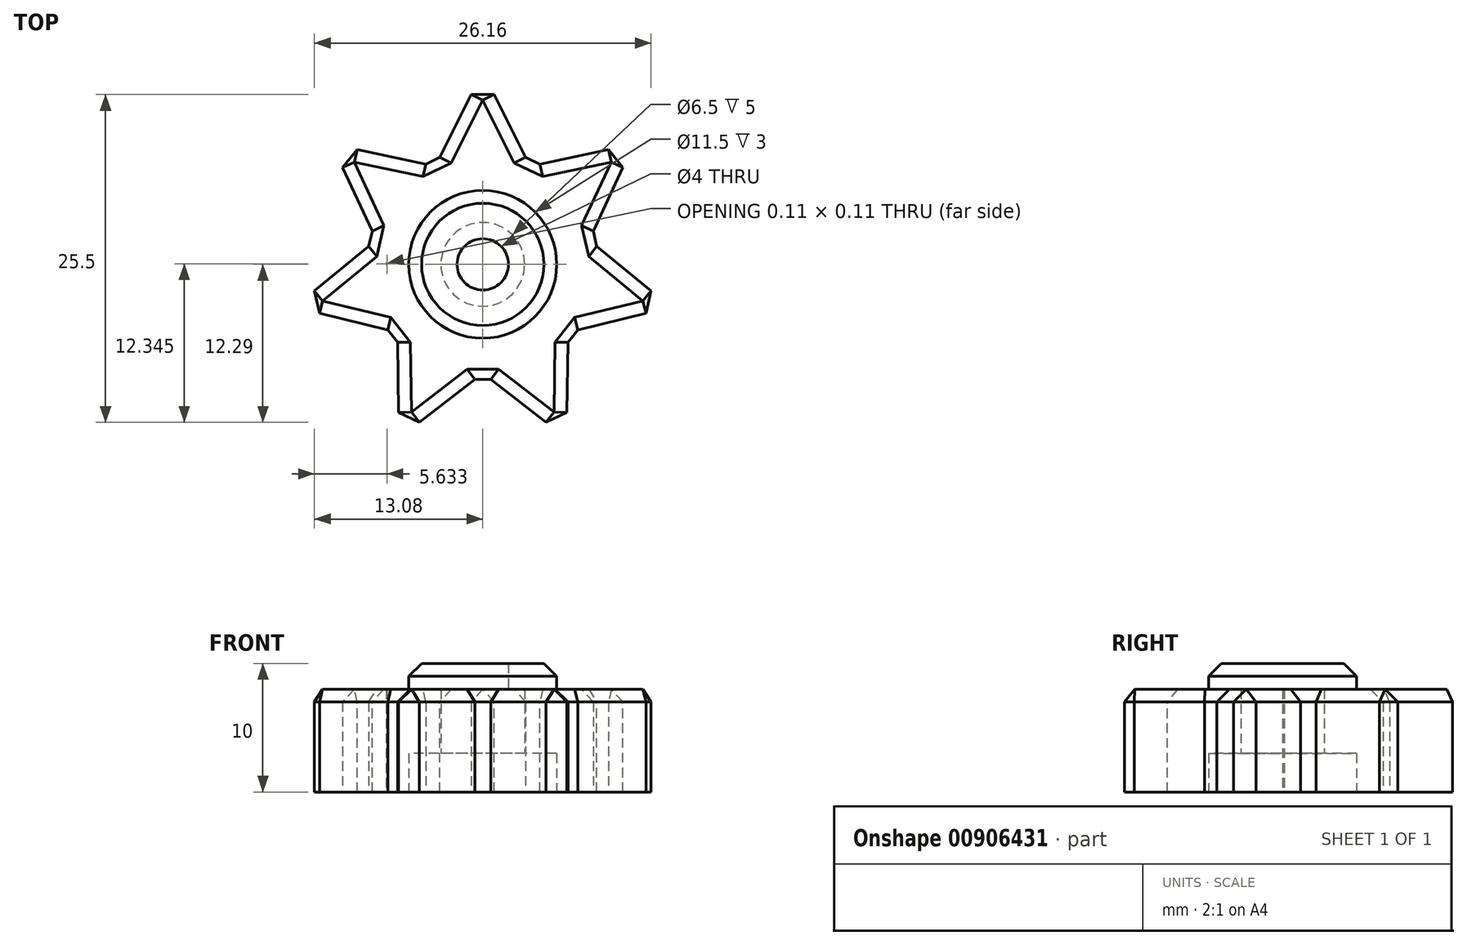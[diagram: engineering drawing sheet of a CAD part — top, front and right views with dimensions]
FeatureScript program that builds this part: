
annotation { "Feature Type Name" : "Feature", "Feature Type Description" : "" }
export const myFeature = defineFeature(function(context is Context, id is Id, definition is map)
    precondition{}
    {
        {
            var Q0;
            Q0=qCreatedBy(makeId("Top.planeOp"),FACE);
            var sketch = newSketch(context, id + "F0", { "sketchPlane" : qUnion([Q0])});
            skLineSegment(sketch, "E0", {"start": v(-7.5, 0) * mm, "end": v(-7.44, 0.11) * mm});
            skLineSegment(sketch, "E1", {"start": v(0, 15) * mm, "end": v(3.68, 7.64) * mm});
            skLineSegment(sketch, "E2.1.0", {"start": v(-4.68, -5.86) * mm, "end": v(-4.73, -5.75) * mm});
            skLineSegment(sketch, "E2.1.1", {"start": v(-11.73, 9.35) * mm, "end": v(-3.68, 7.64) * mm});
            skLineSegment(sketch, "E2.2.0", {"start": v(1.67, -7.31) * mm, "end": v(1.55, -7.28) * mm});
            skLineSegment(sketch, "E2.2.1", {"start": v(-14.62, -3.34) * mm, "end": v(-8.27, 1.89) * mm});
            skLineSegment(sketch, "E2.3.1", {"start": v(-6.5, -13.51) * mm, "end": v(-6.63, -5.29) * mm});
            skLineSegment(sketch, "E2.4.1", {"start": v(6.5, -13.51) * mm, "end": v(0, -8.48) * mm});
            skLineSegment(sketch, "E2.5.1", {"start": v(14.62, -3.34) * mm, "end": v(6.63, -5.29) * mm});
            skLineSegment(sketch, "E2.6.0", {"start": v(-4.68, 5.86) * mm, "end": v(-4.56, 5.89) * mm});
            skLineSegment(sketch, "E2.6.1", {"start": v(11.73, 9.35) * mm, "end": v(8.27, 1.89) * mm});
            skPoint(sketch, "E2.center", {"position": v(0, 0) * mm});
            skLineSegment(sketch, "E3.trimOffspring", {"start": v(-3.68, 7.64) * mm, "end": v(0, 15) * mm});
            skLineSegment(sketch, "E4.trimOffspring", {"start": v(-1.76, 7.23) * mm, "end": v(-1.67, 7.31) * mm});
            skPoint(sketch, "E5.orphan", {"position": v(-6.76, 3.25) * mm});
            skLineSegment(sketch, "E6.trimOffspring", {"start": v(-7.4, 0) * mm, "end": v(-7.44, 0.11) * mm});
            skLineSegment(sketch, "E7.trimOffspring", {"start": v(-8.27, 1.89) * mm, "end": v(-11.73, 9.35) * mm});
            skLineSegment(sketch, "E8.trimOffspring", {"start": v(-6.66, -3.33) * mm, "end": v(-6.76, -3.25) * mm});
            skLineSegment(sketch, "E9.trimOffspring", {"start": v(-6.63, -5.29) * mm, "end": v(-14.62, -3.34) * mm});
            skLineSegment(sketch, "E10.trimOffspring", {"start": v(-7.4, 0) * mm, "end": v(-7.5, 0) * mm});
            skLineSegment(sketch, "E11.trimOffspring", {"start": v(6.63, -5.29) * mm, "end": v(6.5, -13.51) * mm});
            skLineSegment(sketch, "E12.trimOffspring", {"start": v(7.44, 0.11) * mm, "end": v(7.4, 0) * mm});
            skLineSegment(sketch, "E13.trimOffspring", {"start": v(8.27, 1.89) * mm, "end": v(14.62, -3.34) * mm});
            skLineSegment(sketch, "E14.trimOffspring", {"start": v(3.68, 7.64) * mm, "end": v(11.73, 9.35) * mm});
            skLineSegment(sketch, "E15.trimOffspring", {"start": v(4.56, 5.89) * mm, "end": v(4.68, 5.86) * mm});
            skLineSegment(sketch, "E16.trimOffspring", {"start": v(4.73, -5.75) * mm, "end": v(4.68, -5.86) * mm});
            skLineSegment(sketch, "E17.trimOffspring", {"start": v(0, -8.48) * mm, "end": v(-6.5, -13.51) * mm});
            skLineSegment(sketch, "E18.trimOffspring", {"start": v(-1.55, -7.28) * mm, "end": v(-1.67, -7.31) * mm});
            skPoint(sketch, "E19.start.orphan", {"position": v(7.5, 0) * mm});
            skSolve(sketch);
        }
        {
            var Q0;
            Q0=makeQuery(id+"F0.imprint","IMPRINT",FACE,{"disambiguationData":[TD([[makeQuery(id+"F0.imprint","IMPRINT",EDGE,{"derivedFrom":sQuery(id+"F0.wireOp",EDGE,"E0")}),1.0]])]});
            extrude(context, id + "F1", {"entities" : qUnion([Q0]), "depth" : 8 * mm, "offsetDistance" : 25 * mm});
        }
        {
            var Q0;
            Q0=qCreatedBy(makeId("Top.planeOp"),FACE);
            var sketch = newSketch(context, id + "F2", { "sketchPlane" : qUnion([Q0])});
            skCircle(sketch, "E20", {"center": v(0, 0) * mm, "radius": 3.25 * mm});
            skSolve(sketch);
        }
        {
            var Q0;
            Q0=makeQuery(id+"F2.imprint","IMPRINT",FACE,{"disambiguationData":[TD([[makeQuery(id+"F2.imprint","IMPRINT",EDGE,{"derivedFrom":sQuery(id+"F2.wireOp",EDGE,"E20")}),1.0]])]});
            extrude(context, id + "F3", {"entities" : qUnion([Q0]), "operationType" : NewBodyOperationType.REMOVE, "depth" : 25 * mm, "offsetDistance" : 25 * mm});
        }
        {
            var Q0;
            Q0=qCreatedBy(makeId("Top.planeOp"),FACE);
            var sketch = newSketch(context, id + "F4", { "sketchPlane" : qUnion([Q0])});
            skCircle(sketch, "E21", {"center": v(0, 0) * mm, "radius": 5.75 * mm});
            skSolve(sketch);
        }
        {
            var Q0;
            Q0=makeQuery(id+"F4.imprint","IMPRINT",FACE,{"disambiguationData":[TD([[makeQuery(id+"F4.imprint","IMPRINT",EDGE,{"derivedFrom":sQuery(id+"F4.wireOp",EDGE,"E21")}),1.0]])]});
            extrude(context, id + "F5", {"entities" : qUnion([Q0]), "operationType" : NewBodyOperationType.REMOVE, "depth" : 3 * mm, "offsetDistance" : 25 * mm});
        }
        {
            var Q0;
            Q0=qCreatedBy(makeId("Top.planeOp"),FACE);
            cPlane(context, id + "F6", {"entities" : qUnion([Q0]), "cplaneType" : CPlaneType.OFFSET, "offset" : 8 * mm, "width" : 150 * mm, "height" : 150 * mm});
        }
        {
            var Q0;
            Q0=qCreatedBy(id+"F6.planeOp",FACE);
            var sketch = newSketch(context, id + "F7", { "sketchPlane" : qUnion([Q0])});
            skCircle(sketch, "E22", {"center": v(0, 0) * mm, "radius": 5.75 * mm});
            skSolve(sketch);
        }
        {
            var Q0;
            Q0=makeQuery(id+"F7.imprint","IMPRINT",FACE,{"disambiguationData":[TD([[makeQuery(id+"F7.imprint","IMPRINT",EDGE,{"derivedFrom":sQuery(id+"F7.wireOp",EDGE,"E22")}),1.0]])]});
            extrude(context, id + "F8", {"entities" : qUnion([Q0]), "operationType" : NewBodyOperationType.ADD, "depth" : 2 * mm, "offsetDistance" : 25 * mm});
        }
        {
            var Q0;
            Q0=qCreatedBy(id+"F6.planeOp",FACE);
            var sketch = newSketch(context, id + "F9", { "sketchPlane" : qUnion([Q0])});
            skCircle(sketch, "E23", {"center": v(0, 0) * mm, "radius": 2 * mm});
            skSolve(sketch);
        }
        {
            var Q0;
            Q0=makeQuery(id+"F9.imprint","IMPRINT",FACE,{"disambiguationData":[TD([[makeQuery(id+"F9.imprint","IMPRINT",EDGE,{"derivedFrom":sQuery(id+"F9.wireOp",EDGE,"E23")}),1.0]])]});
            var Q1;
            Q1=sQuery(id+"F9.wireOp",EDGE,"E23");
            extrude(context, id + "F10", {"entities" : qUnion([Q0]), "operationType" : NewBodyOperationType.REMOVE, "surfaceEntities" : qUnion([Q1]), "depth" : 25 * mm, "offsetDistance" : 25 * mm});
        }
        {
            var Q0;
            Q0=makeQuery(id+"F1.opExtrude","SWEPT_EDGE",EDGE,{"disambiguationData":[OSD([sQuery(id+"F0.wireOp",EDGE,"E2.5.1"),sQuery(id+"F0.wireOp",EDGE,"E13.trimOffspring")])]});
            var Q1;
            Q1=makeQuery(id+"F1.opExtrude","SWEPT_EDGE",EDGE,{"disambiguationData":[OSD([sQuery(id+"F0.wireOp",EDGE,"E2.6.1"),sQuery(id+"F0.wireOp",EDGE,"E14.trimOffspring")])]});
            var Q2;
            Q2=makeQuery(id+"F1.opExtrude","SWEPT_EDGE",EDGE,{"disambiguationData":[OSD([sQuery(id+"F0.wireOp",EDGE,"E1"),sQuery(id+"F0.wireOp",EDGE,"E3.trimOffspring")])]});
            var Q3;
            Q3=makeQuery(id+"F1.opExtrude","SWEPT_EDGE",EDGE,{"disambiguationData":[OSD([sQuery(id+"F0.wireOp",EDGE,"E2.1.1"),sQuery(id+"F0.wireOp",EDGE,"E7.trimOffspring")])]});
            var Q4;
            Q4=makeQuery(id+"F1.opExtrude","SWEPT_EDGE",EDGE,{"disambiguationData":[OSD([sQuery(id+"F0.wireOp",EDGE,"E2.2.1"),sQuery(id+"F0.wireOp",EDGE,"E9.trimOffspring")])]});
            var Q5;
            Q5=makeQuery(id+"F1.opExtrude","SWEPT_EDGE",EDGE,{"disambiguationData":[OSD([sQuery(id+"F0.wireOp",EDGE,"E2.3.1"),sQuery(id+"F0.wireOp",EDGE,"E17.trimOffspring")])]});
            var Q6;
            Q6=makeQuery(id+"F1.opExtrude","SWEPT_EDGE",EDGE,{"disambiguationData":[OSD([sQuery(id+"F0.wireOp",EDGE,"E2.4.1"),sQuery(id+"F0.wireOp",EDGE,"E11.trimOffspring")])]});
            var Q7;
            Q7=makeQuery(id+"F1.opExtrude","CAP_EDGE",EDGE,{"disambiguationData":[OSD([sQuery(id+"F0.wireOp",EDGE,"E3.trimOffspring")])],"isStart":false});
            var Q8;
            Q8=makeQuery(id+"F1.opExtrude","CAP_EDGE",EDGE,{"disambiguationData":[OSD([sQuery(id+"F0.wireOp",EDGE,"E1")])],"isStart":false});
            var Q9;
            Q9=makeQuery(id+"F1.opExtrude","CAP_EDGE",EDGE,{"disambiguationData":[OSD([sQuery(id+"F0.wireOp",EDGE,"E14.trimOffspring")])],"isStart":false});
            var Q10;
            Q10=makeQuery(id+"F1.opExtrude","CAP_EDGE",EDGE,{"disambiguationData":[OSD([sQuery(id+"F0.wireOp",EDGE,"E2.6.1")])],"isStart":false});
            var Q11;
            Q11=makeQuery(id+"F1.opExtrude","CAP_EDGE",EDGE,{"disambiguationData":[OSD([sQuery(id+"F0.wireOp",EDGE,"E2.1.1")])],"isStart":false});
            var Q12;
            Q12=makeQuery(id+"F1.opExtrude","CAP_EDGE",EDGE,{"disambiguationData":[OSD([sQuery(id+"F0.wireOp",EDGE,"E7.trimOffspring")])],"isStart":false});
            var Q13;
            Q13=makeQuery(id+"F1.opExtrude","CAP_EDGE",EDGE,{"disambiguationData":[OSD([sQuery(id+"F0.wireOp",EDGE,"E2.2.1")])],"isStart":false});
            var Q14;
            Q14=makeQuery(id+"F1.opExtrude","CAP_EDGE",EDGE,{"disambiguationData":[OSD([sQuery(id+"F0.wireOp",EDGE,"E9.trimOffspring")])],"isStart":false});
            var Q15;
            Q15=makeQuery(id+"F1.opExtrude","CAP_EDGE",EDGE,{"disambiguationData":[OSD([sQuery(id+"F0.wireOp",EDGE,"E2.3.1")])],"isStart":false});
            var Q16;
            Q16=makeQuery(id+"F1.opExtrude","CAP_EDGE",EDGE,{"disambiguationData":[OSD([sQuery(id+"F0.wireOp",EDGE,"E17.trimOffspring")])],"isStart":false});
            var Q17;
            Q17=makeQuery(id+"F1.opExtrude","CAP_EDGE",EDGE,{"disambiguationData":[OSD([sQuery(id+"F0.wireOp",EDGE,"E2.4.1")])],"isStart":false});
            var Q18;
            Q18=makeQuery(id+"F1.opExtrude","CAP_EDGE",EDGE,{"disambiguationData":[OSD([sQuery(id+"F0.wireOp",EDGE,"E11.trimOffspring")])],"isStart":false});
            var Q19;
            Q19=makeQuery(id+"F1.opExtrude","CAP_EDGE",EDGE,{"disambiguationData":[OSD([sQuery(id+"F0.wireOp",EDGE,"E2.5.1")])],"isStart":false});
            var Q20;
            Q20=makeQuery(id+"F1.opExtrude","CAP_EDGE",EDGE,{"disambiguationData":[OSD([sQuery(id+"F0.wireOp",EDGE,"E13.trimOffspring")])],"isStart":false});
            var Q21;
            Q21=makeQuery(id+"F8.opExtrude","CAP_EDGE",EDGE,{"disambiguationData":[OSD([sQuery(id+"F7.wireOp",EDGE,"E22")])],"isStart":false});
            var Q22;
            Q22=makeQuery(id+"F1.opExtrude","SWEPT_EDGE",EDGE,{"disambiguationData":[OSD([sQuery(id+"F0.wireOp",EDGE,"E2.1.1"),sQuery(id+"F0.wireOp",EDGE,"E3.trimOffspring")])]});
            var Q23;
            Q23=makeQuery(id+"F1.opExtrude","SWEPT_EDGE",EDGE,{"disambiguationData":[OSD([sQuery(id+"F0.wireOp",EDGE,"E2.2.1"),sQuery(id+"F0.wireOp",EDGE,"E7.trimOffspring")])]});
            var Q24;
            Q24=makeQuery(id+"F1.opExtrude","SWEPT_EDGE",EDGE,{"disambiguationData":[OSD([sQuery(id+"F0.wireOp",EDGE,"E2.3.1"),sQuery(id+"F0.wireOp",EDGE,"E9.trimOffspring")])]});
            var Q25;
            Q25=makeQuery(id+"F1.opExtrude","SWEPT_EDGE",EDGE,{"disambiguationData":[OSD([sQuery(id+"F0.wireOp",EDGE,"E2.4.1"),sQuery(id+"F0.wireOp",EDGE,"E17.trimOffspring")])]});
            var Q26;
            Q26=makeQuery(id+"F1.opExtrude","SWEPT_EDGE",EDGE,{"disambiguationData":[OSD([sQuery(id+"F0.wireOp",EDGE,"E2.5.1"),sQuery(id+"F0.wireOp",EDGE,"E11.trimOffspring")])]});
            var Q27;
            Q27=makeQuery(id+"F1.opExtrude","SWEPT_EDGE",EDGE,{"disambiguationData":[OSD([sQuery(id+"F0.wireOp",EDGE,"E2.6.1"),sQuery(id+"F0.wireOp",EDGE,"E13.trimOffspring")])]});
            var Q28;
            Q28=makeQuery(id+"F1.opExtrude","SWEPT_EDGE",EDGE,{"disambiguationData":[OSD([sQuery(id+"F0.wireOp",EDGE,"E1"),sQuery(id+"F0.wireOp",EDGE,"E14.trimOffspring")])]});
            chamfer(context, id + "F11", {"entities" : qUnion([Q0, Q1, Q2, Q3, Q4, Q5, Q6, Q7, Q8, Q9, Q10, Q11, Q12, Q13, Q14, Q15, Q16, Q17, Q18, Q19, Q20, Q21, Q22, Q23, Q24, Q25, Q26, Q27, Q28]), "width" : 1 * mm, "tangentPropagation" : true});
        }
    });
